# Revit family: 5573IN-0 Family
name_source: partatom
category: Plumbing Fixtures
revit_build: Autodesk Revit 2018 (Build: 20180329_1100(x64)
units: mm (PartAtom-declared; Revit-internal decimal feet)

## family parameters
Cut with Voids When Loaded = No
Host = Face
OmniClass Number = 23.45.05.21.11.11
OmniClass Title = Water Operated Water Closets
Part Type = Normal
Room Calculation Point = No
Round Connector Dimension = Use Radius
Shared = No

## types (5) — shared parameters
CW Connection = Yes
Height = 352 mm
Manufacturer = Kohler
Waste Connection = Yes
Width = 384 mm
zero-valued in all types: CWFU, WFU

## per-type parameters (varying)
| type | Assembly Code | Default Elevation | Description | Material | Model | URL |
| 5573IN-0 |  | 508 mm  [stored 1.66667 ft] | Wall Hung Toilet | Vitreous China | 5573IN-0 Reach | www.us.kohler.com |
| Vitreous_China-7-Black_Black | D2010110 | 1219 mm | Veil one-piece wall-hung toilet | <By Category> | K-6299-7 | http://www.us.kohler.com |
| Vitreous_China-47-Almond | D2010110 | 1219 mm | Veil one-piece wall-hung toilet | <By Category> | K-6299-47 | http://www.us.kohler.com |
| Vitreous_China-96-Biscuit | D2010110 | 1219 mm | Veil one-piece wall-hung toilet | <By Category> | K-6299-96 | http://www.us.kohler.com |
| Vitreous_China-NY-Dune | D2010110 | 1219 mm | Veil one-piece wall-hung toilet | <By Category> | K-6299-NY | http://www.us.kohler.com |

note: [stored X ft] marks values corroborated as IEEE doubles in the binary element streams (Revit-internal decimal feet)

## geometry (parser evidence)
native form markers: Blend x22, Sweep x4
no freeform markers — native parametric forms only
